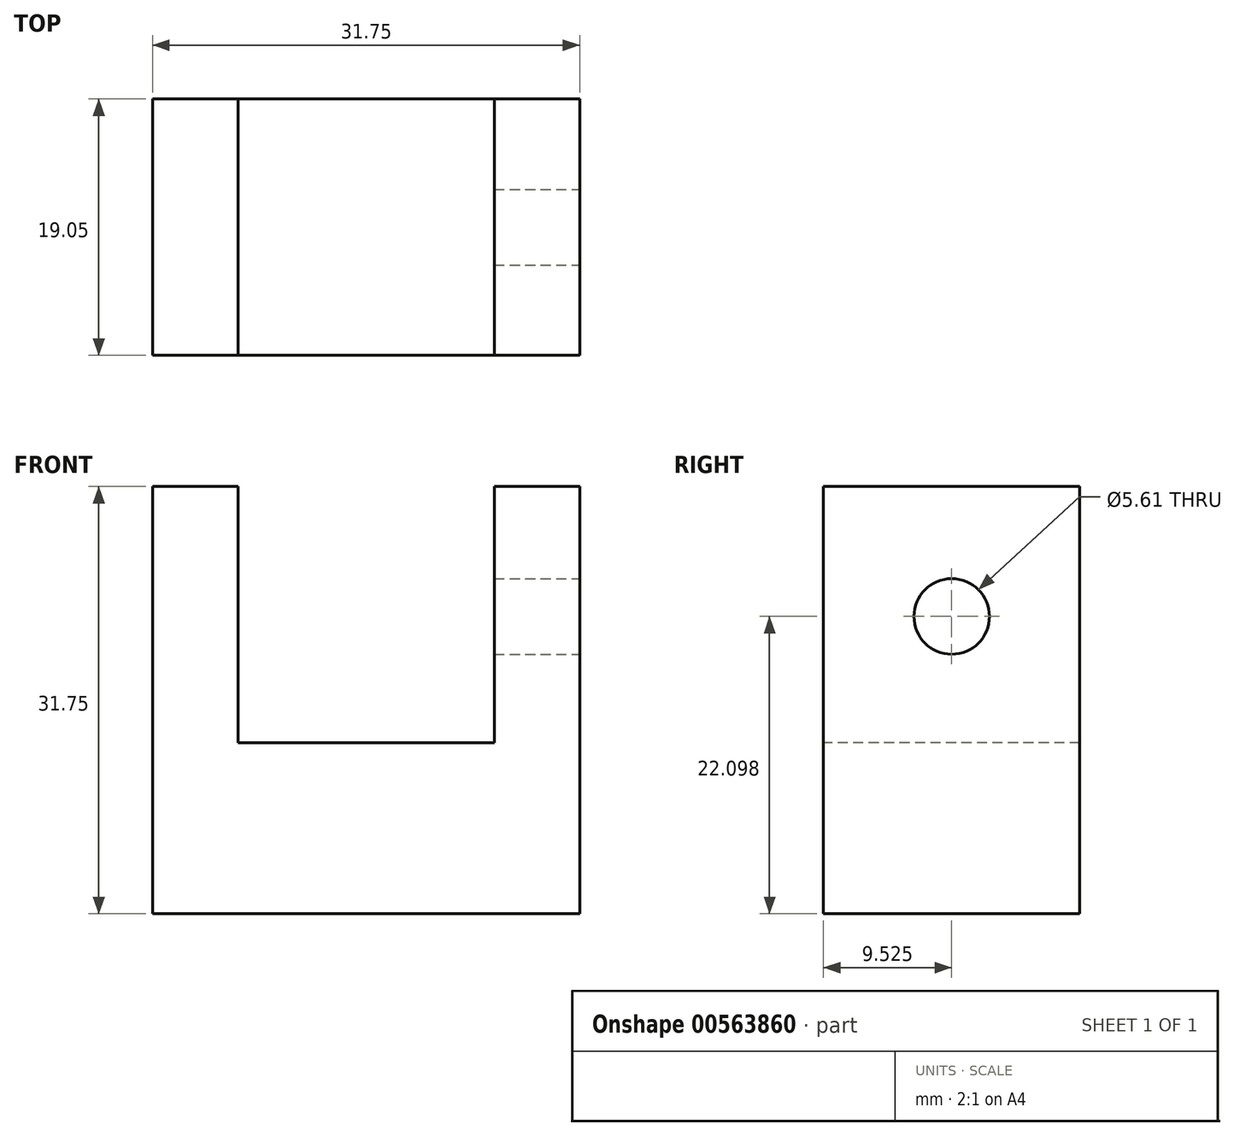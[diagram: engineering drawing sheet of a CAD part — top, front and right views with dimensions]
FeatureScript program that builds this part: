
annotation { "Feature Type Name" : "Feature", "Feature Type Description" : "" }
export const myFeature = defineFeature(function(context is Context, id is Id, definition is map)
    precondition{}
    {
        {
            var Q0;
            Q0=qCreatedBy(makeId("Front.planeOp"),FACE);
            var sketch = newSketch(context, id + "F0", { "sketchPlane" : qUnion([Q0])});
            skLineSegment(sketch, "E0.bottom", {"start": v(0, 0) * mm, "end": v(31.75, 0) * mm});
            skLineSegment(sketch, "E0.top", {"start": v(0, -31.75) * mm, "end": v(31.75, -31.75) * mm});
            skLineSegment(sketch, "E0.left", {"start": v(0, 0) * mm, "end": v(0, -31.75) * mm});
            skLineSegment(sketch, "E0.right", {"start": v(31.75, 0) * mm, "end": v(31.75, -31.75) * mm});
            skSolve(sketch);
        }
        {
            var Q0;
            Q0 = qSketchRegion(id + "F0", true);
            extrude(context, id + "F1", {"entities" : qUnion([Q0]), "depth" : 19.05 * mm, "offsetDistance" : 25.4 * mm});
        }
        {
            var Q0;
            Q0=makeQuery(id+"F1.opExtrude","CAP_FACE",FACE,{"disambiguationData":[OSD([sQuery(id+"F0.wireOp",EDGE,"E0.bottom"),sQuery(id+"F0.wireOp",EDGE,"E0.top"),sQuery(id+"F0.wireOp",EDGE,"E0.left"),sQuery(id+"F0.wireOp",EDGE,"E0.right")])],"isStart":false});
            var sketch = newSketch(context, id + "F2", { "sketchPlane" : qUnion([Q0])});
            skLineSegment(sketch, "E1.bottom", {"start": v(6.35, 0) * mm, "end": v(25.4, 0) * mm});
            skLineSegment(sketch, "E1.top", {"start": v(6.35, -19.05) * mm, "end": v(25.4, -19.05) * mm});
            skLineSegment(sketch, "E1.left", {"start": v(6.35, 0) * mm, "end": v(6.35, -19.05) * mm});
            skLineSegment(sketch, "E1.right", {"start": v(25.4, 0) * mm, "end": v(25.4, -19.05) * mm});
            skSolve(sketch);
        }
        {
            var Q0;
            Q0 = qSketchRegion(id + "F2", true);
            extrude(context, id + "F3", {"entities" : qUnion([Q0]), "operationType" : NewBodyOperationType.REMOVE, "endBound" : BoundingType.THROUGH_ALL, "oppositeDirection" : true, "depth" : 25.4 * mm, "offsetDistance" : 25.4 * mm});
        }
        {
            var Q0;
            Q0=makeQuery(id+"F1.opExtrude","SWEPT_FACE",FACE,{"disambiguationData":[OSD([sQuery(id+"F0.wireOp",EDGE,"E0.right")])]});
            var sketch = newSketch(context, id + "F4", { "sketchPlane" : qUnion([Q0])});
            skPoint(sketch, "E2", {"position": v(-9.53, -9.65) * mm});
            skSolve(sketch);
        }
        {
            var Q0;
            Q0=sQuery(id+"F4.wireOp",VERTEX,"E2");
            var Q1;
            Q1=makeQuery(id+"F1.opExtrude","SWEPT_BODY",BODY,{"disambiguationData":[OSD([sQuery(id+"F0.wireOp",EDGE,"E0.bottom"),sQuery(id+"F0.wireOp",EDGE,"E0.top"),sQuery(id+"F0.wireOp",EDGE,"E0.left"),sQuery(id+"F0.wireOp",EDGE,"E0.right")])]});
            hole(context, id + "F5", {"style" : HoleStyle.SIMPLE, "endStyle" : HoleEndStyle.BLIND, "holeDiameter" : 5.61 * mm, "holeDepth" : 7.62 * mm, "isTappedThrough" : true, "tappedDepth" : 12.7 * mm, "tapClearance" : 3, "startFromSketch" : true, "locations" : qUnion([Q0]), "scope" : qUnion([Q1])});
        }
    });
